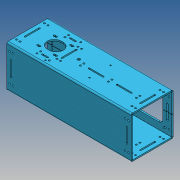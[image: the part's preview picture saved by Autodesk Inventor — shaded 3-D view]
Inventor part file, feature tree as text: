
AUTODESK INVENTOR PART (.ipt)
format: ipt  version: 2017 (Build 210142000, 142)  size: 801,792 bytes
history: native  units: mm
features: other x15, sketch x6, extrude x5, plane x1, projected_geometry x1
ambient origin geometry x8: Origin, YZ Plane, XZ Plane, XY Plane, X Axis, Y Axis, Z Axis, Center Point
bodies: Body1 (feature_tree)
feature tree (28):
  other  "Sólido1"
  extrude  "Extrusión1"  Depth=67.5mm
  other  "Pestaña1"
  sketch  "Boceto4"  dims[d9=41.14mm d10=6.0mm]
  other  "Cara1"
  other  "Cara2"
  extrude  "Extrusión4"  Depth=42.0mm
  sketch  "Boceto5"  dims[d11=53.14mm d12=6.0mm]
  other  "Cara3"
  plane  "Plano de trabajo1"
  extrude  "Extrusión5"  Depth=5.0mm
  extrude  "Extrusión3"  Depth=6.0mm
  extrude  "Extrusión2"  Depth=6.0mm
  sketch  "Boceto1"  dims[d1=56.4mm d2=67.5mm]
  sketch  "Boceto2"  dims[d4=200.0mm d5=42.0mm]
  other  "Placa1"
  other  "Doblez1"
  other  "Esquina1"
  sketch  "Boceto3"  dims[d6=8.0mm d8=5.0mm]
  projected_geometry  "Contorno proyectado1"
  other  "Placa2"
  other  "Doblez2"
  other  "Placa3"
  other  "Doblez3"
  other  "Placa4"
  other  "Doblez4"
  sketch  "Boceto6"  dims[d13=4.0mm d14=115.0mm d15=20.0mm d16=60.0mm d17=60.0mm d18=4.0mm d19=33.93mm d20=22.0mm d21=120.0mm d22=130.0mm d23=20.0mm d24=4.0mm d25=0.0mm d26=4.0mm d27=2.0mm d28=8.0mm d29=4.0mm d30=120.0mm d31=90.0deg d32=0.1mm d33=16.0mm d34=4.0mm d35=4.0mm d36=4.0mm d37=8.0mm d38=25.0mm d39=25.0mm d40=4.0mm d41=0.0mm d42=47.14mm d43=47.14mm d44=20.0mm d45=6.0mm d46=14.2mm d47=25.0mm d48=0.1mm d49=4.0mm d50=2.0mm d51=8.0mm d52=4.0mm d53=0.1mm d54=4.0mm d55=2.0mm d56=8.0mm d57=4.0mm d58=0.5mm d59=0.5mm d60=20.0mm d61=24.0mm d62=4.0mm d63=41.0mm d65=5.0mm d66=10.0mm d67=5.0mm d68=40.0mm d70=4.0mm d71=60.0mm d72=25.0mm d73=0.1mm d74=4.0mm d75=2.0mm d76=8.0mm d77=4.0mm d78=4.0mm d79=41.0mm d80=55.75mm d81=59.75mm d82=84.0mm d83=5.0mm d84=20.0mm d85=0.0mm d86=50.0mm d87=355.0mm d88=12.5mm d89=12.5mm d90=23.6mm d91=11.8mm d92=15.0mm d93=20.0mm d94=80.0mm d95=40.0mm d96=4.0mm d97=194.8mm d98=97.4mm d99=10.0mm d100=10.0mm d101=60.0mm d102=12.0mm d103=0.25mm d104=5.0mm d105=8.0mm d106=3.0mm d107=8.0mm d108=3.0mm d109=12.5mm d110=10.0mm d111=40.0mm d112=5.0mm d113=10.0mm d114=0.0mm d115=10.0mm d116=0.0mm]
  other  "Definición1"
